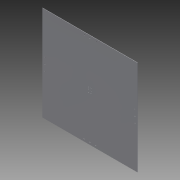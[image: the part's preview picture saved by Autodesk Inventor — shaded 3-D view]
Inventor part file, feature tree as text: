
AUTODESK INVENTOR PART (.ipt)
format: ipt  version: 2014 (Build 180170000, 170)  size: 110,080 bytes
history: native  units: in
note: dims shown in document units (in); Inventor stores cm internally (conversion verified against a paired STEP export)
features: extrude x1, sketch x1
ambient origin geometry x8: Origin, YZ Plane, XZ Plane, XY Plane, X Axis, Y Axis, Z Axis, Center Point
bodies: Solid1 (feature_tree)
feature tree (2):
  extrude  "Extrusion1"  Depth=20.0in
  sketch  "Sketch1"  dims[d0=20.0in d1=20.0in d16=0.0625in d17=0.0in d18=1.0in d19=1.5in d20=0.196in d21=0.25in d22=0.25in d23=0.7874in d25=0.5in d26=1.1811in d28=0.5in d31=0.75in d32=3.0in d33=0.196in d34=0.25in d35=0.25in d36=0.25in d37=1.5748in d39=360.0deg]
